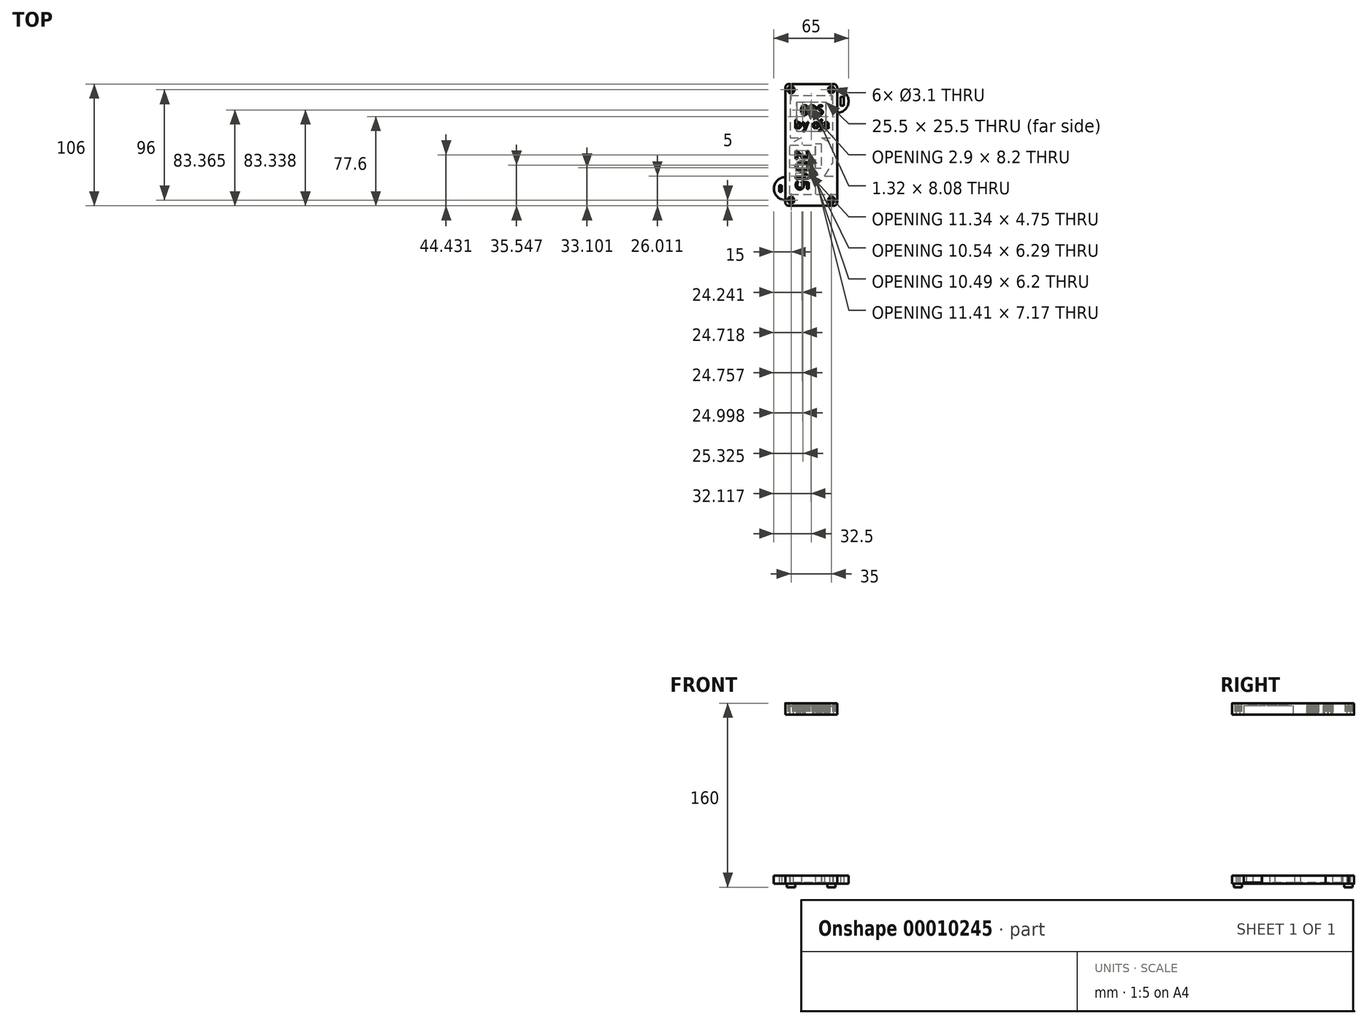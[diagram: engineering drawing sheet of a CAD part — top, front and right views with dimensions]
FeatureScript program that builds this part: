
annotation { "Feature Type Name" : "Feature", "Feature Type Description" : "" }
export const myFeature = defineFeature(function(context is Context, id is Id, definition is map)
    precondition{}
    {
        {
            var Q0;
            Q0=qCreatedBy(makeId("Top.planeOp"),FACE);
            var sketch = newSketch(context, id + "F0", { "sketchPlane" : qUnion([Q0])});
            skLineSegment(sketch, "E0.rect.bottom", {"start": v(19.5, 53) * mm, "end": v(-19.5, 53) * mm});
            skLineSegment(sketch, "E0.rect.top", {"start": v(19.5, -53) * mm, "end": v(-19.5, -53) * mm});
            skLineSegment(sketch, "E0.rect.left", {"start": v(22.5, 50) * mm, "end": v(22.5, -50) * mm});
            skLineSegment(sketch, "E0.rect.right", {"start": v(-22.5, 50) * mm, "end": v(-22.5, -50) * mm});
            skPoint(sketch, "E0.rect.middle", {"position": v(0, 0) * mm});
            skLineSegment(sketch, "E1.bottom", {"start": v(-18.5, -43) * mm, "end": v(3.5, -43) * mm});
            skLineSegment(sketch, "E1.top", {"start": v(-18.5, 1) * mm, "end": v(3.5, 1) * mm});
            skLineSegment(sketch, "E1.left", {"start": v(-18.5, -43) * mm, "end": v(-18.5, 1) * mm});
            skLineSegment(sketch, "E1.right", {"start": v(3.5, -43) * mm, "end": v(3.5, 1) * mm});
            skLineSegment(sketch, "E2.bottom", {"start": v(8.5, 1) * mm, "end": v(18.5, 1) * mm});
            skLineSegment(sketch, "E2.top", {"start": v(8.5, -16) * mm, "end": v(18.5, -16) * mm});
            skLineSegment(sketch, "E2.left", {"start": v(8.5, 1) * mm, "end": v(8.5, -16) * mm});
            skLineSegment(sketch, "E2.right", {"start": v(18.5, 1) * mm, "end": v(18.5, -16) * mm});
            skLineSegment(sketch, "E3.bottom", {"start": v(-18.4, 43) * mm, "end": v(18.4, 43) * mm});
            skLineSegment(sketch, "E3.top", {"start": v(-18.4, 6.2) * mm, "end": v(18.4, 6.2) * mm});
            skLineSegment(sketch, "E3.left", {"start": v(-18.4, 43) * mm, "end": v(-18.4, 6.2) * mm});
            skLineSegment(sketch, "E3.right", {"start": v(18.4, 43) * mm, "end": v(18.4, 6.2) * mm});
            skLineSegment(sketch, "E4", {"start": v(0, 6.2) * mm, "end": v(0, 43) * mm, "construction": true});
            skLineSegment(sketch, "E5", {"start": v(22.5, -43) * mm, "end": v(11.5, -43) * mm});
            skLineSegment(sketch, "E6", {"start": v(11.5, -43) * mm, "end": v(11.5, -27) * mm});
            skLineSegment(sketch, "E7", {"start": v(11.5, -27) * mm, "end": v(22.5, -27) * mm});
            skCircle(sketch, "E8", {"center": v(-17.5, 48) * mm, "radius": 1.55 * mm});
            skCircle(sketch, "E9.0.MirrorC", {"center": v(17.5, 48) * mm, "radius": 1.55 * mm});
            skCircle(sketch, "E10.0.MirrorC", {"center": v(17.5, -48) * mm, "radius": 1.55 * mm});
            skCircle(sketch, "E10.1.MirrorC", {"center": v(-17.5, -48) * mm, "radius": 1.55 * mm});
            skLineSegment(sketch, "E11.rect.bottom", {"start": v(12.75, 11.85) * mm, "end": v(-12.75, 11.85) * mm});
            skLineSegment(sketch, "E11.rect.top", {"start": v(12.75, 37.35) * mm, "end": v(-12.75, 37.35) * mm});
            skLineSegment(sketch, "E11.rect.left", {"start": v(12.75, 11.85) * mm, "end": v(12.75, 37.35) * mm});
            skLineSegment(sketch, "E11.rect.right", {"start": v(-12.75, 11.85) * mm, "end": v(-12.75, 37.35) * mm});
            skPoint(sketch, "E11.rect.middle", {"position": v(0, 24.6) * mm});
            skArc(sketch, "E12", {"start": v(22.5, 28) * mm, "mid": v(32.5, 38) * mm, "end": v(22.5, 48) * mm});
            skArc(sketch, "E13", {"start": v(-22.5, -28) * mm, "mid": v(-32.5, -38) * mm, "end": v(-22.5, -48) * mm});
            skLineSegment(sketch, "E14.rect.bottom", {"start": v(25.56, 34.16) * mm, "end": v(28.23, 34.16) * mm});
            skLineSegment(sketch, "E14.rect.top", {"start": v(25.56, 41.84) * mm, "end": v(28.23, 41.84) * mm});
            skLineSegment(sketch, "E14.rect.left", {"start": v(25.56, 34.16) * mm, "end": v(25.56, 41.84) * mm});
            skLineSegment(sketch, "E14.rect.right", {"start": v(28.23, 34.16) * mm, "end": v(28.23, 41.84) * mm});
            skPoint(sketch, "E14.rect.middle", {"position": v(26.9, 38) * mm});
            skLineSegment(sketch, "E15.rect.bottom", {"start": v(-25.72, -40.9) * mm, "end": v(-27.78, -40.9) * mm});
            skLineSegment(sketch, "E15.rect.top", {"start": v(-25.72, -35.1) * mm, "end": v(-27.78, -35.1) * mm});
            skLineSegment(sketch, "E15.rect.left", {"start": v(-25.72, -40.9) * mm, "end": v(-25.72, -35.1) * mm});
            skLineSegment(sketch, "E15.rect.right", {"start": v(-27.78, -40.9) * mm, "end": v(-27.78, -35.1) * mm});
            skPoint(sketch, "E15.rect.middle", {"position": v(-26.75, -38) * mm});
            skFitSpline(sketch, "E16", {"points": [v(-8.47, 6.2) * mm, v(-18.5, 1) * mm], "startDerivative": vector(-10.03, -5.2) * mm, "endDerivative": vector(-10.03, -5.2) * mm});
            skFitSpline(sketch, "E17", {"points": [v(9, 6.2) * mm, v(18.5, 1) * mm], "startDerivative": vector(9.5, -5.2) * mm, "endDerivative": vector(9.5, -5.2) * mm});
            skFitSpline(sketch, "E18", {"points": [v(11.5, -27) * mm, v(18.5, -16) * mm], "startDerivative": vector(7, 11) * mm, "endDerivative": vector(7, 11) * mm});
            skLineSegment(sketch, "E19", {"start": v(3.5, 1) * mm, "end": v(8.5, 1) * mm});
            skLineSegment(sketch, "E20", {"start": v(11.5, -43) * mm, "end": v(3.5, -43) * mm});
            skLineSegment(sketch, "E21", {"start": v(8.5, -16) * mm, "end": v(8.5, -20.46) * mm});
            skLineSegment(sketch, "E22", {"start": v(8.5, -20.46) * mm, "end": v(3.5, -20.46) * mm});
            skPoint(sketch, "E23.visualSharp", {"position": v(-22.5, 53) * mm});
            skArc(sketch, "E23.filletArc", {"start": v(-19.5, 53) * mm, "mid": v(-21.62, 52.12) * mm, "end": v(-22.5, 50) * mm});
            skPoint(sketch, "E24.visualSharp", {"position": v(22.5, 53) * mm});
            skArc(sketch, "E24.filletArc", {"start": v(22.5, 50) * mm, "mid": v(21.62, 52.12) * mm, "end": v(19.5, 53) * mm});
            skPoint(sketch, "E25.visualSharp", {"position": v(22.5, -53) * mm});
            skArc(sketch, "E25.filletArc", {"start": v(19.5, -53) * mm, "mid": v(21.62, -52.12) * mm, "end": v(22.5, -50) * mm});
            skPoint(sketch, "E26.visualSharp", {"position": v(-22.5, -53) * mm});
            skArc(sketch, "E26.filletArc", {"start": v(-22.5, -50) * mm, "mid": v(-21.62, -52.12) * mm, "end": v(-19.5, -53) * mm});
            skSolve(sketch);
        }
        {
            var Q0;
            {var subQ3=sQuery(id+"F0.wireOp",EDGE,"E0.rect.bottom");Q0=makeQuery(id+"F0.imprint","IMPRINT",FACE,{"disambiguationData":[TD([[makeQuery(id+"F0.imprint","IMPRINT",EDGE,{"derivedFrom":subQ3}),1.0]])]});}
            var Q1;
            {var subQ0=sQuery(id+"F0.wireOp",EDGE,"E13");Q1=makeQuery(id+"F0.imprint","IMPRINT",FACE,{"disambiguationData":[TD([[makeQuery(id+"F0.imprint","IMPRINT",EDGE,{"derivedFrom":subQ0}),1.0]])]});}
            var Q2;
            {var subQ0=sQuery(id+"F0.wireOp",EDGE,"E12");Q2=makeQuery(id+"F0.imprint","IMPRINT",FACE,{"disambiguationData":[TD([[makeQuery(id+"F0.imprint","IMPRINT",EDGE,{"derivedFrom":subQ0}),1.0]])]});}
            var Q3;
            Q3=makeQuery(id+"F0.imprint","IMPRINT",FACE,{"disambiguationData":[TD([[makeQuery(id+"F0.imprint","IMPRINT",EDGE,{"derivedFrom":sQuery(id+"F0.wireOp",EDGE,"E2.left")}),-1.0]])]});
            extrude(context, id + "F1", {"entities" : qUnion([Q0, Q1, Q2, Q3]), "depth" : 10 * mm});
        }
        {
            var Q0;
            Q0=makeQuery(id+"F0.imprint","IMPRINT",FACE,{"disambiguationData":[TD([[makeQuery(id+"F0.imprint","IMPRINT",EDGE,{"derivedFrom":sQuery(id+"F0.wireOp",EDGE,"E3.bottom")}),-1.0]])]});
            var Q1;
            Q1=makeQuery(id+"F0.imprint","IMPRINT",FACE,{"disambiguationData":[TD([[makeQuery(id+"F0.imprint","IMPRINT",EDGE,{"derivedFrom":sQuery(id+"F0.wireOp",EDGE,"E1.bottom")}),1.0]])]});
            var Q2;
            Q2=makeQuery(id+"F0.imprint","IMPRINT",FACE,{"disambiguationData":[TD([[makeQuery(id+"F0.imprint","IMPRINT",EDGE,{"derivedFrom":sQuery(id+"F0.wireOp",EDGE,"E2.bottom")}),-1.0]])]});
            var Q3;
            {var subQ1=sQuery(id+"F0.wireOp",EDGE,"E5");Q3=makeQuery(id+"F0.imprint","IMPRINT",FACE,{"disambiguationData":[TD([[makeQuery(id+"F0.imprint","IMPRINT",EDGE,{"derivedFrom":subQ1}),-1.0]])]});}
            var Q4;
            Q4=makeQuery(id+"F0.imprint","IMPRINT",FACE,{"disambiguationData":[TD([[makeQuery(id+"F0.imprint","IMPRINT",EDGE,{"derivedFrom":sQuery(id+"F0.wireOp",EDGE,"E1.top")}),1.0]])]});
            var Q5;
            Q5=makeQuery(id+"F0.imprint","IMPRINT",FACE,{"disambiguationData":[TD([[makeQuery(id+"F0.imprint","IMPRINT",EDGE,{"derivedFrom":sQuery(id+"F0.wireOp",EDGE,"E2.top")}),-1.0]])]});
            extrude(context, id + "F2", {"entities" : qUnion([Q0, Q1, Q2, Q3, Q4, Q5]), "operationType" : NewBodyOperationType.ADD, "depth" : 4 * mm});
        }
        {
            var Q0;
            Q0=makeQuery(id+"F0.imprint","IMPRINT",FACE,{"disambiguationData":[TD([[makeQuery(id+"F0.imprint","IMPRINT",EDGE,{"derivedFrom":sQuery(id+"F0.wireOp",EDGE,"E11.rect.bottom")}),-1.0]])]});
            extrude(context, id + "F3", {"entities" : qUnion([Q0]), "operationType" : NewBodyOperationType.ADD, "depth" : 2 * mm});
        }
        {
            var Q0;
            Q0=qCreatedBy(makeId("Top.planeOp"),FACE);
            cPlane(context, id + "F4", {"entities" : qUnion([Q0]), "cplaneType" : CPlaneType.OFFSET, "offset" : 150 * mm, "width" : 150 * mm, "height" : 150 * mm});
        }
        {
            var Q0;
            Q0=qCreatedBy(id+"F4.planeOp",FACE);
            var sketch = newSketch(context, id + "F5", { "sketchPlane" : qUnion([Q0])});
            skLineSegment(sketch, "E27.0", {"start": v(-22.5, 50) * mm, "end": v(-22.5, -50) * mm});
            skArc(sketch, "E28.0", {"start": v(-19.5, 53) * mm, "mid": v(-21.62, 52.12) * mm, "end": v(-22.5, 50) * mm});
            skLineSegment(sketch, "E29.0", {"start": v(19.5, 53) * mm, "end": v(-19.5, 53) * mm});
            skArc(sketch, "E30.0", {"start": v(22.5, 50) * mm, "mid": v(21.62, 52.12) * mm, "end": v(19.5, 53) * mm});
            skLineSegment(sketch, "E31.0", {"start": v(22.5, 50) * mm, "end": v(22.5, -50) * mm});
            skArc(sketch, "E32.0", {"start": v(19.5, -53) * mm, "mid": v(21.62, -52.12) * mm, "end": v(22.5, -50) * mm});
            skLineSegment(sketch, "E33.0", {"start": v(19.5, -53) * mm, "end": v(-19.5, -53) * mm});
            skArc(sketch, "E34.0", {"start": v(-22.5, -50) * mm, "mid": v(-21.62, -52.12) * mm, "end": v(-19.5, -53) * mm});
            skCircle(sketch, "E35.0", {"center": v(-17.5, -48) * mm, "radius": 1.55 * mm});
            skCircle(sketch, "E36.0", {"center": v(17.5, -48) * mm, "radius": 1.55 * mm});
            skCircle(sketch, "E37.0", {"center": v(-17.5, 48) * mm, "radius": 1.55 * mm});
            skCircle(sketch, "E38.0", {"center": v(17.5, 48) * mm, "radius": 1.55 * mm});
            skCircle(sketch, "E39.cCircle", {"center": v(-17.5, 48) * mm, "radius": 2.75 * mm, "construction": true});
            skLineSegment(sketch, "E39.0", {"start": v(-14.36, 48.5) * mm, "end": v(-15.5, 45.53) * mm});
            skLineSegment(sketch, "E39.1", {"start": v(-15.5, 45.53) * mm, "end": v(-18.64, 45.04) * mm});
            skLineSegment(sketch, "E39.2", {"start": v(-18.64, 45.04) * mm, "end": v(-20.64, 47.5) * mm});
            skLineSegment(sketch, "E39.3", {"start": v(-20.64, 47.5) * mm, "end": v(-19.5, 50.47) * mm});
            skLineSegment(sketch, "E39.4", {"start": v(-19.5, 50.47) * mm, "end": v(-16.36, 50.96) * mm});
            skLineSegment(sketch, "E39.5", {"start": v(-16.36, 50.96) * mm, "end": v(-14.36, 48.5) * mm});
            skPoint(sketch, "E39.0.midPoint", {"position": v(-14.93, 47.01) * mm});
            skCircle(sketch, "E40.cCircle", {"center": v(17.5, 48) * mm, "radius": 2.78 * mm, "construction": true});
            skLineSegment(sketch, "E40.0", {"start": v(20.67, 48.51) * mm, "end": v(19.53, 45.51) * mm});
            skLineSegment(sketch, "E40.1", {"start": v(19.53, 45.51) * mm, "end": v(16.36, 45) * mm});
            skLineSegment(sketch, "E40.2", {"start": v(16.36, 45) * mm, "end": v(14.33, 47.49) * mm});
            skLineSegment(sketch, "E40.3", {"start": v(14.33, 47.49) * mm, "end": v(15.47, 50.49) * mm});
            skLineSegment(sketch, "E40.4", {"start": v(15.47, 50.49) * mm, "end": v(18.64, 51) * mm});
            skLineSegment(sketch, "E40.5", {"start": v(18.64, 51) * mm, "end": v(20.67, 48.51) * mm});
            skPoint(sketch, "E40.0.midPoint", {"position": v(20.1, 47.01) * mm});
            skCircle(sketch, "E41.cCircle", {"center": v(-17.5, -48) * mm, "radius": 2.75 * mm, "construction": true});
            skLineSegment(sketch, "E41.0", {"start": v(-14.37, -47.46) * mm, "end": v(-15.46, -50.44) * mm});
            skLineSegment(sketch, "E41.1", {"start": v(-15.46, -50.44) * mm, "end": v(-18.6, -50.98) * mm});
            skLineSegment(sketch, "E41.2", {"start": v(-18.6, -50.98) * mm, "end": v(-20.63, -48.54) * mm});
            skLineSegment(sketch, "E41.3", {"start": v(-20.63, -48.54) * mm, "end": v(-19.54, -45.56) * mm});
            skLineSegment(sketch, "E41.4", {"start": v(-19.54, -45.56) * mm, "end": v(-16.4, -45.02) * mm});
            skLineSegment(sketch, "E41.5", {"start": v(-16.4, -45.02) * mm, "end": v(-14.37, -47.46) * mm});
            skPoint(sketch, "E41.0.midPoint", {"position": v(-14.92, -48.95) * mm});
            skCircle(sketch, "E42.cCircle", {"center": v(17.5, -48) * mm, "radius": 2.75 * mm, "construction": true});
            skLineSegment(sketch, "E42.0", {"start": v(14.36, -47.54) * mm, "end": v(16.33, -45.05) * mm});
            skLineSegment(sketch, "E42.1", {"start": v(16.33, -45.05) * mm, "end": v(19.47, -45.5) * mm});
            skLineSegment(sketch, "E42.2", {"start": v(19.47, -45.5) * mm, "end": v(20.64, -48.46) * mm});
            skLineSegment(sketch, "E42.3", {"start": v(20.64, -48.46) * mm, "end": v(18.67, -50.95) * mm});
            skLineSegment(sketch, "E42.4", {"start": v(18.67, -50.95) * mm, "end": v(15.53, -50.5) * mm});
            skLineSegment(sketch, "E42.5", {"start": v(15.53, -50.5) * mm, "end": v(14.36, -47.54) * mm});
            skPoint(sketch, "E42.0.midPoint", {"position": v(15.34, -46.3) * mm});
            skText(sketch, "E43", { "text": "2015", "fontName": "AllertaStencil-Regular.ttf"});
            skText(sketch, "E44", { "text": "GPS", "fontName": "AllertaStencil-Regular.ttf"});
            skText(sketch, "E45", { "text": "by oja", "fontName": "AllertaStencil-Regular.ttf"});
            skLineSegment(sketch, "E46.bottom", {"start": v(-18.52, -43) * mm, "end": v(3.86, -43) * mm});
            skLineSegment(sketch, "E46.top", {"start": v(-18.52, 0) * mm, "end": v(3.86, 0) * mm});
            skLineSegment(sketch, "E46.left", {"start": v(-18.52, -43) * mm, "end": v(-18.52, 0) * mm});
            skLineSegment(sketch, "E46.right", {"start": v(3.86, -43) * mm, "end": v(3.86, 0) * mm});
            const initialGuessF5  = {"E43": [-0.01345, -0.00377, 0, -1, 0.01134], "E44": [-0.00982, 0.0263, 1, 0, 0.00808], "E45": [-0.01466, 0.01434, 1, 0, 0.00713]};
            skSetInitialGuess(sketch, initialGuessF5);
            skSolve(sketch);
        }
        {
            var Q0;
            Q0=makeQuery(id+"F5.imprint","IMPRINT",FACE,{"disambiguationData":[TD([[makeQuery(id+"F5.imprint","IMPRINT",EDGE,{"derivedFrom":sQuery(id+"F5.wireOp",EDGE,"E27.0")}),1.0]])]});
            var Q1;
            Q1=makeQuery(id+"F5.imprint","IMPRINT",FACE,{"disambiguationData":[TD([[makeQuery(id+"F5.imprint","IMPRINT",EDGE,{"derivedFrom":sQuery(id+"F5.wireOp",EDGE,"2cab86c5-86d5-46c9-8b4e-2d4a3fcfca98.sketch_text.stroke-28")}),1.0]])]});
            var Q2;
            Q2=makeQuery(id+"F5.imprint","IMPRINT",FACE,{"disambiguationData":[TD([[makeQuery(id+"F5.imprint","IMPRINT",EDGE,{"derivedFrom":sQuery(id+"F5.wireOp",EDGE,"fed3cacc-00c7-4c0d-a1d3-4be8ef2b1fc1.sketch_text.stroke-15")}),1.0]])]});
            var Q3;
            Q3=makeQuery(id+"F5.imprint","IMPRINT",FACE,{"disambiguationData":[TD([[makeQuery(id+"F5.imprint","IMPRINT",EDGE,{"derivedFrom":sQuery(id+"F5.wireOp",EDGE,"fed3cacc-00c7-4c0d-a1d3-4be8ef2b1fc1.sketch_text.stroke-47")}),1.0]])]});
            var Q4;
            Q4=makeQuery(id+"F5.imprint","IMPRINT",FACE,{"disambiguationData":[TD([[makeQuery(id+"F5.imprint","IMPRINT",EDGE,{"derivedFrom":sQuery(id+"F5.wireOp",EDGE,"fed3cacc-00c7-4c0d-a1d3-4be8ef2b1fc1.sketch_text.stroke-73")}),1.0]])]});
            var Q5;
            Q5=makeQuery(id+"F5.imprint","IMPRINT",FACE,{"disambiguationData":[TD([[makeQuery(id+"F5.imprint","IMPRINT",EDGE,{"derivedFrom":sQuery(id+"F5.wireOp",EDGE,"E43.sketch_text.stroke-0")}),1.0]])]});
            extrude(context, id + "F6", {"entities" : qUnion([Q0, Q1, Q2, Q3, Q4, Q5]), "depth" : 10 * mm});
        }
        {
            var Q0;
            Q0=makeQuery(id+"F5.imprint","IMPRINT",FACE,{"disambiguationData":[TD([[makeQuery(id+"F5.imprint","IMPRINT",EDGE,{"derivedFrom":sQuery(id+"F5.wireOp",EDGE,"E35.0")}),1.0]])]});
            var Q1;
            Q1=makeQuery(id+"F5.imprint","IMPRINT",FACE,{"disambiguationData":[TD([[makeQuery(id+"F5.imprint","IMPRINT",EDGE,{"derivedFrom":sQuery(id+"F5.wireOp",EDGE,"E36.0")}),-1.0]])]});
            var Q2;
            Q2=makeQuery(id+"F5.imprint","IMPRINT",FACE,{"disambiguationData":[TD([[makeQuery(id+"F5.imprint","IMPRINT",EDGE,{"derivedFrom":sQuery(id+"F5.wireOp",EDGE,"E37.0")}),-1.0]])]});
            var Q3;
            Q3=makeQuery(id+"F5.imprint","IMPRINT",FACE,{"disambiguationData":[TD([[makeQuery(id+"F5.imprint","IMPRINT",EDGE,{"derivedFrom":sQuery(id+"F5.wireOp",EDGE,"E38.0")}),1.0]])]});
            var Q4;
            Q4=makeQuery(id+"F5.imprint","IMPRINT",FACE,{"disambiguationData":[TD([[makeQuery(id+"F5.imprint","IMPRINT",EDGE,{"derivedFrom":sQuery(id+"F5.wireOp",EDGE,"2cab86c5-86d5-46c9-8b4e-2d4a3fcfca98.sketch_text.stroke-0")}),-1.0]])]});
            var Q5;
            Q5=makeQuery(id+"F5.imprint","IMPRINT",FACE,{"disambiguationData":[TD([[makeQuery(id+"F5.imprint","IMPRINT",EDGE,{"derivedFrom":sQuery(id+"F5.wireOp",EDGE,"2cab86c5-86d5-46c9-8b4e-2d4a3fcfca98.sketch_text.stroke-35")}),-1.0]])]});
            var Q6;
            Q6=makeQuery(id+"F5.imprint","IMPRINT",FACE,{"disambiguationData":[TD([[makeQuery(id+"F5.imprint","IMPRINT",EDGE,{"derivedFrom":sQuery(id+"F5.wireOp",EDGE,"2cab86c5-86d5-46c9-8b4e-2d4a3fcfca98.sketch_text.stroke-20")}),-1.0]])]});
            var Q7;
            Q7=makeQuery(id+"F5.imprint","IMPRINT",FACE,{"disambiguationData":[TD([[makeQuery(id+"F5.imprint","IMPRINT",EDGE,{"derivedFrom":sQuery(id+"F5.wireOp",EDGE,"fed3cacc-00c7-4c0d-a1d3-4be8ef2b1fc1.sketch_text.stroke-0")}),-1.0]])]});
            var Q8;
            Q8=makeQuery(id+"F5.imprint","IMPRINT",FACE,{"disambiguationData":[TD([[makeQuery(id+"F5.imprint","IMPRINT",EDGE,{"derivedFrom":sQuery(id+"F5.wireOp",EDGE,"fed3cacc-00c7-4c0d-a1d3-4be8ef2b1fc1.sketch_text.stroke-23")}),-1.0]])]});
            var Q9;
            Q9=makeQuery(id+"F5.imprint","IMPRINT",FACE,{"disambiguationData":[TD([[makeQuery(id+"F5.imprint","IMPRINT",EDGE,{"derivedFrom":sQuery(id+"F5.wireOp",EDGE,"fed3cacc-00c7-4c0d-a1d3-4be8ef2b1fc1.sketch_text.stroke-39")}),-1.0]])]});
            var Q10;
            Q10=makeQuery(id+"F5.imprint","IMPRINT",FACE,{"disambiguationData":[TD([[makeQuery(id+"F5.imprint","IMPRINT",EDGE,{"derivedFrom":sQuery(id+"F5.wireOp",EDGE,"fed3cacc-00c7-4c0d-a1d3-4be8ef2b1fc1.sketch_text.stroke-55")}),-1.0]])]});
            var Q11;
            Q11=makeQuery(id+"F5.imprint","IMPRINT",FACE,{"disambiguationData":[TD([[makeQuery(id+"F5.imprint","IMPRINT",EDGE,{"derivedFrom":sQuery(id+"F5.wireOp",EDGE,"fed3cacc-00c7-4c0d-a1d3-4be8ef2b1fc1.sketch_text.stroke-65")}),-1.0]])]});
            extrude(context, id + "F7", {"entities" : qUnion([Q0, Q1, Q2, Q3, Q4, Q5, Q6, Q7, Q8, Q9, Q10, Q11]), "operationType" : NewBodyOperationType.ADD, "depth" : 7.5 * mm});
        }
        {
            var Q0;
            Q0=makeQuery(id+"F5.imprint","IMPRINT",FACE,{"disambiguationData":[TD([[makeQuery(id+"F5.imprint","IMPRINT",EDGE,{"derivedFrom":sQuery(id+"F5.wireOp",EDGE,"E43.sketch_text.stroke-0")}),1.0]])]});
            extrude(context, id + "F8", {"entities" : qUnion([Q0]), "operationType" : NewBodyOperationType.REMOVE, "depth" : 8 * mm});
        }
        {
            var Q0;
            {var subQ0=sQuery(id+"F0.wireOp",EDGE,"E0.rect.left");var subQ1=sQuery(id+"F0.wireOp",EDGE,"E1.bottom");var subQ2=sQuery(id+"F0.wireOp",EDGE,"E1.left");var subQ3=sQuery(id+"F0.wireOp",EDGE,"E2.right");var subQ4=sQuery(id+"F0.wireOp",EDGE,"E3.bottom");var subQ5=sQuery(id+"F0.wireOp",EDGE,"E3.top");var subQ6=sQuery(id+"F0.wireOp",EDGE,"E3.left");var subQ7=sQuery(id+"F0.wireOp",EDGE,"E3.right");var subQ8=sQuery(id+"F0.wireOp",EDGE,"E5");var subQ9=sQuery(id+"F0.wireOp",EDGE,"E7");var subQ10=sQuery(id+"F0.wireOp",EDGE,"E16");var subQ11=sQuery(id+"F0.wireOp",EDGE,"E17");var subQ12=sQuery(id+"F0.wireOp",EDGE,"E18");var subQ13=sQuery(id+"F0.wireOp",EDGE,"E20");var subQ14=sQuery(id+"F0.wireOp",EDGE,"E1.right");var subQ15=sQuery(id+"F0.wireOp",EDGE,"E2.left");var subQ16=sQuery(id+"F0.wireOp",EDGE,"E19");var subQ17=sQuery(id+"F0.wireOp",EDGE,"E21");var subQ18=sQuery(id+"F0.wireOp",EDGE,"E22");var subQ19=sQuery(id+"F0.wireOp",EDGE,"E11.rect.bottom");var subQ20=sQuery(id+"F0.wireOp",EDGE,"E11.rect.top");var subQ21=sQuery(id+"F0.wireOp",EDGE,"E11.rect.left");var subQ22=sQuery(id+"F0.wireOp",EDGE,"E11.rect.right");Q0=makeQuery(id+"F3.boolean.opBoolean","MERGE",FACE,{"derivedFrom":[makeQuery(id+"F2.boolean.opBoolean","MERGE",FACE,{"derivedFrom":[makeQuery(id+"F1.opExtrude","CAP_FACE",FACE,{"disambiguationData":[OSD([sQuery(id+"F0.wireOp",EDGE,"E0.rect.bottom"),sQuery(id+"F0.wireOp",EDGE,"E0.rect.top"),subQ0,sQuery(id+"F0.wireOp",EDGE,"E0.rect.right"),subQ1,subQ2,subQ3,subQ4,subQ5,subQ6,subQ7,subQ8,subQ9,sQuery(id+"F0.wireOp",EDGE,"E8"),sQuery(id+"F0.wireOp",EDGE,"E9.0.MirrorC"),sQuery(id+"F0.wireOp",EDGE,"E10.0.MirrorC"),sQuery(id+"F0.wireOp",EDGE,"E10.1.MirrorC"),sQuery(id+"F0.wireOp",EDGE,"E12"),sQuery(id+"F0.wireOp",EDGE,"E13"),sQuery(id+"F0.wireOp",EDGE,"E14.rect.bottom"),sQuery(id+"F0.wireOp",EDGE,"E14.rect.top"),sQuery(id+"F0.wireOp",EDGE,"E14.rect.left"),sQuery(id+"F0.wireOp",EDGE,"E14.rect.right"),sQuery(id+"F0.wireOp",EDGE,"E15.rect.bottom"),sQuery(id+"F0.wireOp",EDGE,"E15.rect.top"),sQuery(id+"F0.wireOp",EDGE,"E15.rect.left"),sQuery(id+"F0.wireOp",EDGE,"E15.rect.right"),subQ10,subQ11,subQ12,subQ13,sQuery(id+"F0.wireOp",EDGE,"E23.filletArc"),sQuery(id+"F0.wireOp",EDGE,"E24.filletArc"),sQuery(id+"F0.wireOp",EDGE,"E25.filletArc"),sQuery(id+"F0.wireOp",EDGE,"E26.filletArc")])],"isStart":true}),makeQuery(id+"F1.opExtrude","CAP_FACE",FACE,{"disambiguationData":[OSD([subQ14,subQ15,subQ16,subQ17,subQ18])],"isStart":true}),makeQuery(id+"F2.opExtrude","CAP_FACE",FACE,{"disambiguationData":[OSD([subQ0,subQ1,subQ2,subQ14,subQ15,subQ3,subQ4,subQ5,subQ6,subQ7,subQ8,subQ9,subQ19,subQ20,subQ21,subQ22,subQ10,subQ11,subQ12,subQ16,subQ13,subQ17,subQ18])],"isStart":true})]}),makeQuery(id+"F3.opExtrude","CAP_FACE",FACE,{"disambiguationData":[OSD([subQ19,subQ20,subQ21,subQ22])],"isStart":true})]});}
            var sketch = newSketch(context, id + "F9", { "sketchPlane" : qUnion([Q0])});
            skCircle(sketch, "E47.0", {"center": v(17.5, -48) * mm, "radius": 3.55 * mm});
            skCircle(sketch, "E48.0", {"center": v(-17.5, -48) * mm, "radius": 3.55 * mm});
            skCircle(sketch, "E49.0", {"center": v(17.5, 48) * mm, "radius": 3.55 * mm});
            skCircle(sketch, "E50.0", {"center": v(-17.5, 48) * mm, "radius": 3.55 * mm});
            skSolve(sketch);
        }
        {
            var Q0;
            Q0=makeQuery(id+"F9.imprint","IMPRINT",FACE,{"disambiguationData":[TD([[makeQuery(id+"F9.imprint","IMPRINT",EDGE,{"derivedFrom":sQuery(id+"F9.wireOp",EDGE,"E50.0")}),1.0]])]});
            var Q1;
            Q1=makeQuery(id+"F9.imprint","IMPRINT",FACE,{"disambiguationData":[TD([[makeQuery(id+"F9.imprint","IMPRINT",EDGE,{"derivedFrom":sQuery(id+"F9.wireOp",EDGE,"E49.0")}),-1.0]])]});
            var Q2;
            Q2=makeQuery(id+"F9.imprint","IMPRINT",FACE,{"disambiguationData":[TD([[makeQuery(id+"F9.imprint","IMPRINT",EDGE,{"derivedFrom":sQuery(id+"F9.wireOp",EDGE,"E47.0")}),1.0]])]});
            var Q3;
            Q3=makeQuery(id+"F9.imprint","IMPRINT",FACE,{"disambiguationData":[TD([[makeQuery(id+"F9.imprint","IMPRINT",EDGE,{"derivedFrom":sQuery(id+"F9.wireOp",EDGE,"E48.0")}),-1.0]])]});
            extrude(context, id + "F10", {"entities" : qUnion([Q0, Q1, Q2, Q3]), "operationType" : NewBodyOperationType.REMOVE, "oppositeDirection" : true, "depth" : 3 * mm});
        }
    });
